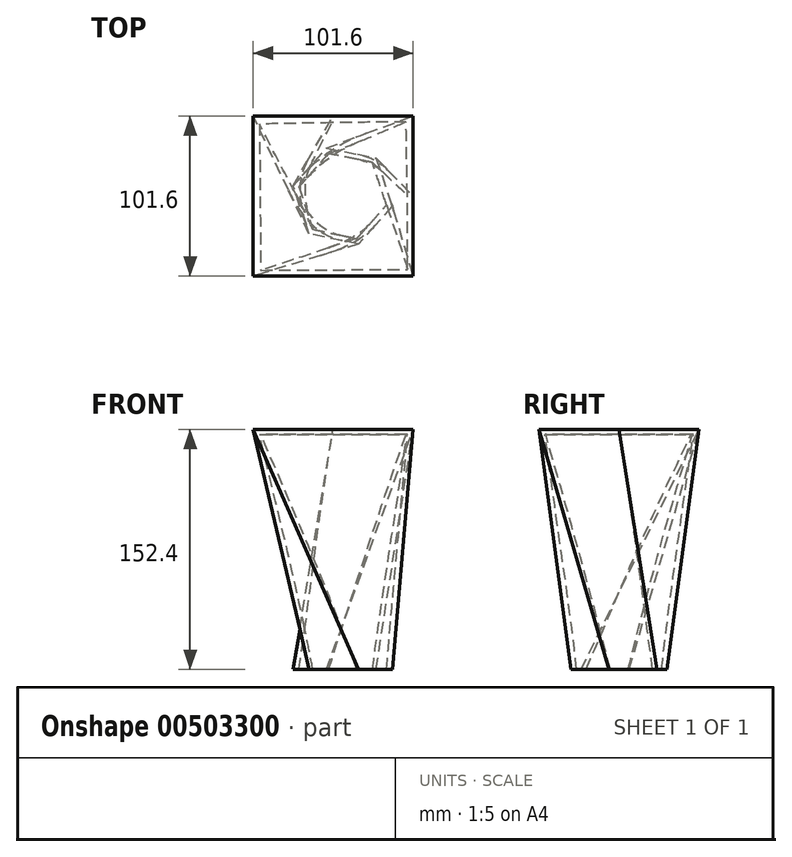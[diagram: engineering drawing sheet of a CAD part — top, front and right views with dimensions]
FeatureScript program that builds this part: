
annotation { "Feature Type Name" : "Feature", "Feature Type Description" : "" }
export const myFeature = defineFeature(function(context is Context, id is Id, definition is map)
    precondition{}
    {
        {
            var Q0;
            Q0=qCreatedBy(makeId("Top.planeOp"),FACE);
            var sketch = newSketch(context, id + "F0", { "sketchPlane" : qUnion([Q0])});
            skCircle(sketch, "E0.cCircle", {"center": v(0, 0) * mm, "radius": 27.84 * mm, "construction": true});
            skLineSegment(sketch, "E0.0", {"start": v(31.5, -6.4) * mm, "end": v(10.2, -30.48) * mm});
            skLineSegment(sketch, "E0.1", {"start": v(10.2, -30.48) * mm, "end": v(-21.3, -24.08) * mm});
            skLineSegment(sketch, "E0.2", {"start": v(-21.3, -24.08) * mm, "end": v(-31.5, 6.4) * mm});
            skLineSegment(sketch, "E0.3", {"start": v(-31.5, 6.4) * mm, "end": v(-10.2, 30.48) * mm});
            skLineSegment(sketch, "E0.4", {"start": v(-10.2, 30.48) * mm, "end": v(21.3, 24.08) * mm});
            skLineSegment(sketch, "E0.5", {"start": v(21.3, 24.08) * mm, "end": v(31.5, -6.4) * mm});
            skPoint(sketch, "E0.0.midPoint", {"position": v(20.85, -18.44) * mm});
            skSolve(sketch);
        }
        {
            var Q0;
            Q0=qCreatedBy(makeId("Top.planeOp"),FACE);
            cPlane(context, id + "F1", {"entities" : qUnion([Q0]), "cplaneType" : CPlaneType.OFFSET, "offset" : 152.4 * mm, "width" : 152.4 * mm, "height" : 152.4 * mm});
        }
        {
            var Q0;
            Q0=qCreatedBy(id+"F1.planeOp",FACE);
            var sketch = newSketch(context, id + "F2", { "sketchPlane" : qUnion([Q0])});
            skLineSegment(sketch, "E1.bottom", {"start": v(44.75, -50.8) * mm, "end": v(-56.85, -50.8) * mm});
            skLineSegment(sketch, "E1.top", {"start": v(44.75, 50.8) * mm, "end": v(-56.85, 50.8) * mm});
            skLineSegment(sketch, "E1.left", {"start": v(44.75, -50.8) * mm, "end": v(44.75, 50.8) * mm});
            skLineSegment(sketch, "E1.right", {"start": v(-56.85, -50.8) * mm, "end": v(-56.85, 50.8) * mm});
            skPoint(sketch, "E1.middle", {"position": v(-6.05, 0) * mm});
            skSolve(sketch);
        }
        {
            var Q0;
            Q0=makeQuery(id+"F0.imprint","IMPRINT",FACE,{"disambiguationData":[TD([[makeQuery(id+"F0.imprint","IMPRINT",EDGE,{"derivedFrom":sQuery(id+"F0.wireOp",EDGE,"E0.0")}),-1.0]])]});
            var Q1;
            Q1=makeQuery(id+"F2.imprint","IMPRINT",FACE,{"disambiguationData":[TD([[makeQuery(id+"F2.imprint","IMPRINT",EDGE,{"derivedFrom":sQuery(id+"F2.wireOp",EDGE,"E1.bottom")}),-1.0]])]});
            loft(context, id + "F3", {"sheetProfilesArray" : [{ "sheetProfileEntities" : qUnion([Q0]) }, { "sheetProfileEntities" : qUnion([Q1]) }]});
        }
        {
            var Q0;
            Q0=makeQuery(id+"F3.opLoft","CAP_FACE",FACE,{"disambiguationData":[OSD([makeQuery(id+"F0.imprint","IMPRINT",FACE,{"disambiguationData":[TD([[makeQuery(id+"F0.imprint","IMPRINT",EDGE,{"derivedFrom":sQuery(id+"F0.wireOp",EDGE,"E0.0")}),-1.0]])]})])],"isStart":true});
            shell(context, id + "F4", {"entities" : qUnion([Q0]), "thickness" : 3.17 * mm});
        }
    });
